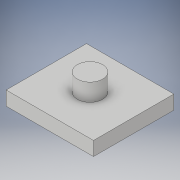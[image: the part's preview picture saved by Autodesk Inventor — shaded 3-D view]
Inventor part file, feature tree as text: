
AUTODESK INVENTOR PART (.ipt)
format: ipt  version: 2018 (Build 220112000, 112)  size: 101,888 bytes
history: native  units: in
note: dims shown in document units (in); Inventor stores cm internally (conversion verified against a paired STEP export)
features: extrude x2, sketch x2
ambient origin geometry x8: Origin, YZ Plane, XZ Plane, XY Plane, X Axis, Y Axis, Z Axis, Center Point
bodies: Solid1 (feature_tree)
feature tree (4):
  extrude  "Extrusion1"  Depth=0.9055in
  extrude  "Extrusion2"  Depth=0.1969in
  sketch  "Sketch1"  dims[d0=0.9843in d1=0.9055in]
  sketch  "Sketch2"  dims[d2=0.1575in d3=0.0in d4=0.2846in d5=0.4921in d6=0.4528in d7=0.1969in d8=0.0in]
